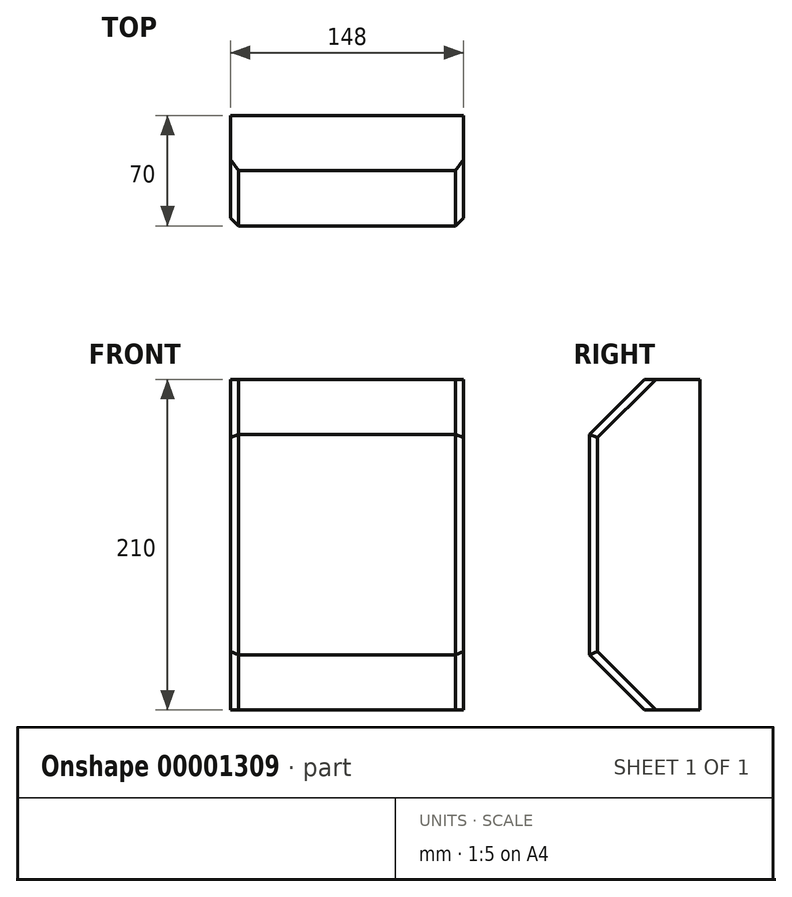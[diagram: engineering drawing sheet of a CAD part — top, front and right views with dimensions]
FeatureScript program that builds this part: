
annotation { "Feature Type Name" : "Feature", "Feature Type Description" : "" }
export const myFeature = defineFeature(function(context is Context, id is Id, definition is map)
    precondition{}
    {
        {
            var Q0;
            Q0=qCreatedBy(makeId("Front.planeOp"),FACE);
            var sketch = newSketch(context, id + "F0", { "sketchPlane" : qUnion([Q0])});
            skLineSegment(sketch, "E0.bottom", {"start": v(-105, -74) * mm, "end": v(43, -74) * mm});
            skLineSegment(sketch, "E0.top", {"start": v(-105, 136) * mm, "end": v(43, 136) * mm});
            skLineSegment(sketch, "E0.left", {"start": v(-105, -74) * mm, "end": v(-105, 136) * mm});
            skLineSegment(sketch, "E0.right", {"start": v(43, -74) * mm, "end": v(43, 136) * mm});
            skSolve(sketch);
        }
        {
            var Q0;
            Q0=makeQuery(id+"F0.imprint","IMPRINT",FACE,{"disambiguationData":[TD([[makeQuery(id+"F0.imprint","IMPRINT",EDGE,{"derivedFrom":sQuery(id+"F0.wireOp",EDGE,"E0.bottom")}),1.0]])]});
            extrude(context, id + "F1", {"entities" : qUnion([Q0]), "depth" : 70 * mm, "offsetDistance" : 25 * mm});
        }
        {
            var Q0;
            Q0=makeQuery(id+"F1.opExtrude","CAP_EDGE",EDGE,{"disambiguationData":[OSD([sQuery(id+"F0.wireOp",EDGE,"E0.top")])],"isStart":false});
            var Q1;
            Q1=makeQuery(id+"F1.opExtrude","CAP_EDGE",EDGE,{"disambiguationData":[OSD([sQuery(id+"F0.wireOp",EDGE,"E0.bottom")])],"isStart":false});
            chamfer(context, id + "F2", {"entities" : qUnion([Q0, Q1]), "width" : 35 * mm, "tangentPropagation" : true});
        }
        {
            var Q0;
            Q0=makeQuery(id+"F1.opExtrude","CAP_EDGE",EDGE,{"disambiguationData":[OSD([sQuery(id+"F0.wireOp",EDGE,"E0.right")])],"isStart":false});
            var Q1;
            Q1=makeQuery(id+"F1.opExtrude","CAP_EDGE",EDGE,{"disambiguationData":[OSD([sQuery(id+"F0.wireOp",EDGE,"E0.left")])],"isStart":false});
            var Q2;
            Q2=makeQuery(id+"F2.opChamfer","BLEND_EDGE",EDGE,{"blendedFrom":[makeQuery(id+"F1.opExtrude","CAP_EDGE",EDGE,{"disambiguationData":[OSD([sQuery(id+"F0.wireOp",EDGE,"E0.top")])],"isStart":false}),makeQuery(id+"F1.opExtrude","SWEPT_FACE",FACE,{"disambiguationData":[OSD([sQuery(id+"F0.wireOp",EDGE,"E0.left")])]})],"blendedInto":[makeQuery(id+"F1.opExtrude","SWEPT_FACE",FACE,{"disambiguationData":[OSD([sQuery(id+"F0.wireOp",EDGE,"E0.left")])]})]});
            var Q3;
            Q3=makeQuery(id+"F2.opChamfer","BLEND_EDGE",EDGE,{"blendedFrom":[makeQuery(id+"F1.opExtrude","CAP_EDGE",EDGE,{"disambiguationData":[OSD([sQuery(id+"F0.wireOp",EDGE,"E0.top")])],"isStart":false}),makeQuery(id+"F1.opExtrude","SWEPT_FACE",FACE,{"disambiguationData":[OSD([sQuery(id+"F0.wireOp",EDGE,"E0.right")])]})],"blendedInto":[makeQuery(id+"F1.opExtrude","SWEPT_FACE",FACE,{"disambiguationData":[OSD([sQuery(id+"F0.wireOp",EDGE,"E0.right")])]})]});
            var Q4;
            Q4=makeQuery(id+"F2.opChamfer","BLEND_EDGE",EDGE,{"blendedFrom":[makeQuery(id+"F1.opExtrude","CAP_EDGE",EDGE,{"disambiguationData":[OSD([sQuery(id+"F0.wireOp",EDGE,"E0.bottom")])],"isStart":false}),makeQuery(id+"F1.opExtrude","SWEPT_FACE",FACE,{"disambiguationData":[OSD([sQuery(id+"F0.wireOp",EDGE,"E0.right")])]})],"blendedInto":[makeQuery(id+"F1.opExtrude","SWEPT_FACE",FACE,{"disambiguationData":[OSD([sQuery(id+"F0.wireOp",EDGE,"E0.right")])]})]});
            var Q5;
            Q5=makeQuery(id+"F2.opChamfer","BLEND_EDGE",EDGE,{"blendedFrom":[makeQuery(id+"F1.opExtrude","CAP_EDGE",EDGE,{"disambiguationData":[OSD([sQuery(id+"F0.wireOp",EDGE,"E0.bottom")])],"isStart":false}),makeQuery(id+"F1.opExtrude","SWEPT_FACE",FACE,{"disambiguationData":[OSD([sQuery(id+"F0.wireOp",EDGE,"E0.left")])]})],"blendedInto":[makeQuery(id+"F1.opExtrude","SWEPT_FACE",FACE,{"disambiguationData":[OSD([sQuery(id+"F0.wireOp",EDGE,"E0.left")])]})]});
            chamfer(context, id + "F3", {"entities" : qUnion([Q0, Q1, Q2, Q3, Q4, Q5]), "width" : 5 * mm, "tangentPropagation" : true});
        }
    });
